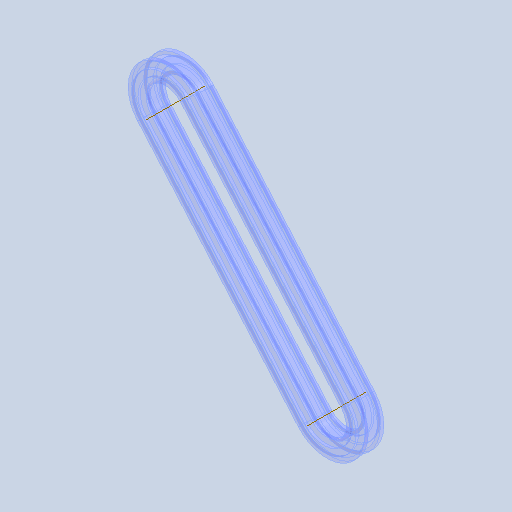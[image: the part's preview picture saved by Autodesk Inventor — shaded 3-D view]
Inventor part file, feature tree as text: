
AUTODESK INVENTOR PART (.ipt)
format: ipt  version: 2022.1 (Build 261234000, 234)  size: 174,080 bytes
history: native  units: mm
features: other x4, plane x2, sweep x1, pattern_linear x1, sketch x1
ambient origin geometry x8: Origin, YZ Plane, XZ Plane, XY Plane, X Axis, Y Axis, Z Axis, Center Point
bodies: Solid1 (feature_tree)
feature tree (9):
  other  "Eje de trabajo1"
  other  "Eje de trabajo2"
  plane  "Plano de trabajo2"
  plane  "Plano de trabajo3"
  other  "Trayectoria"
  other  "Plano de sección"
  sweep  "Sólido"
  pattern_linear  "Strand Pattern"  Spacing1=5.08mm  [1 undecoded]
  sketch  "Boceto de sección"  dims[d2=0.0mm d4=0.0mm d21=5.08mm d22=10.16mm d23=9.65mm d24=3.0mm d28=10.0mm d30=16.59mm d31=14.73mm d32=19.6mm d33=0.0mm d34=0.0mm d35=0.0mm d36=0.0mm d37=0.0mm]
note: 1 required parameter value undecoded (feature->parameter linkage not recoverable at this tier; creation-order binding heuristic only, values carry confidence <= 0.55)
